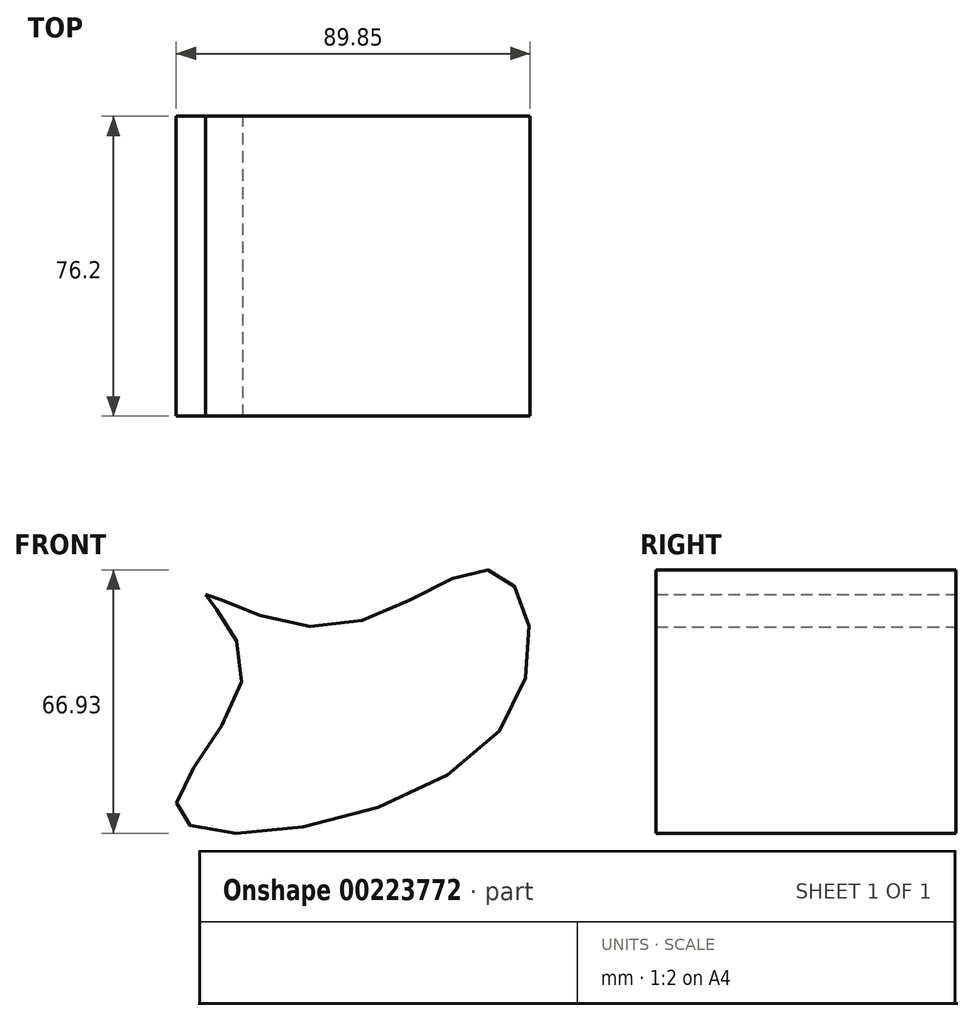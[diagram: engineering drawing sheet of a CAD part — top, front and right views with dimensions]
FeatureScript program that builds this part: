
annotation { "Feature Type Name" : "Feature", "Feature Type Description" : "" }
export const myFeature = defineFeature(function(context is Context, id is Id, definition is map)
    precondition{}
    {
        {
            var Q0;
            Q0=qCreatedBy(makeId("Front.planeOp"),FACE);
            var sketch = newSketch(context, id + "F0", { "sketchPlane" : qUnion([Q0])});
            skFitSpline(sketch, "E0", {"points": [v(-39.95, 36.6) * mm, v(-30.48, 17.43) * mm, v(-46.87, -19.51) * mm, v(33.02, 0) * mm, v(34.17, 42.37) * mm, v(-8.54, 28.52) * mm, v(-39.95, 36.6) * mm]});
            skSolve(sketch);
        }
        {
            var Q0;
            Q0=makeQuery(id+"F0.imprint","IMPRINT",FACE,{"disambiguationData":[TD([[makeQuery(id+"F0.imprint","IMPRINT",EDGE,{"derivedFrom":sQuery(id+"F0.wireOp",EDGE,"E0")}),1.0]])]});
            extrude(context, id + "F1", {"entities" : qUnion([Q0]), "depth" : 76.2 * mm});
        }
    });
